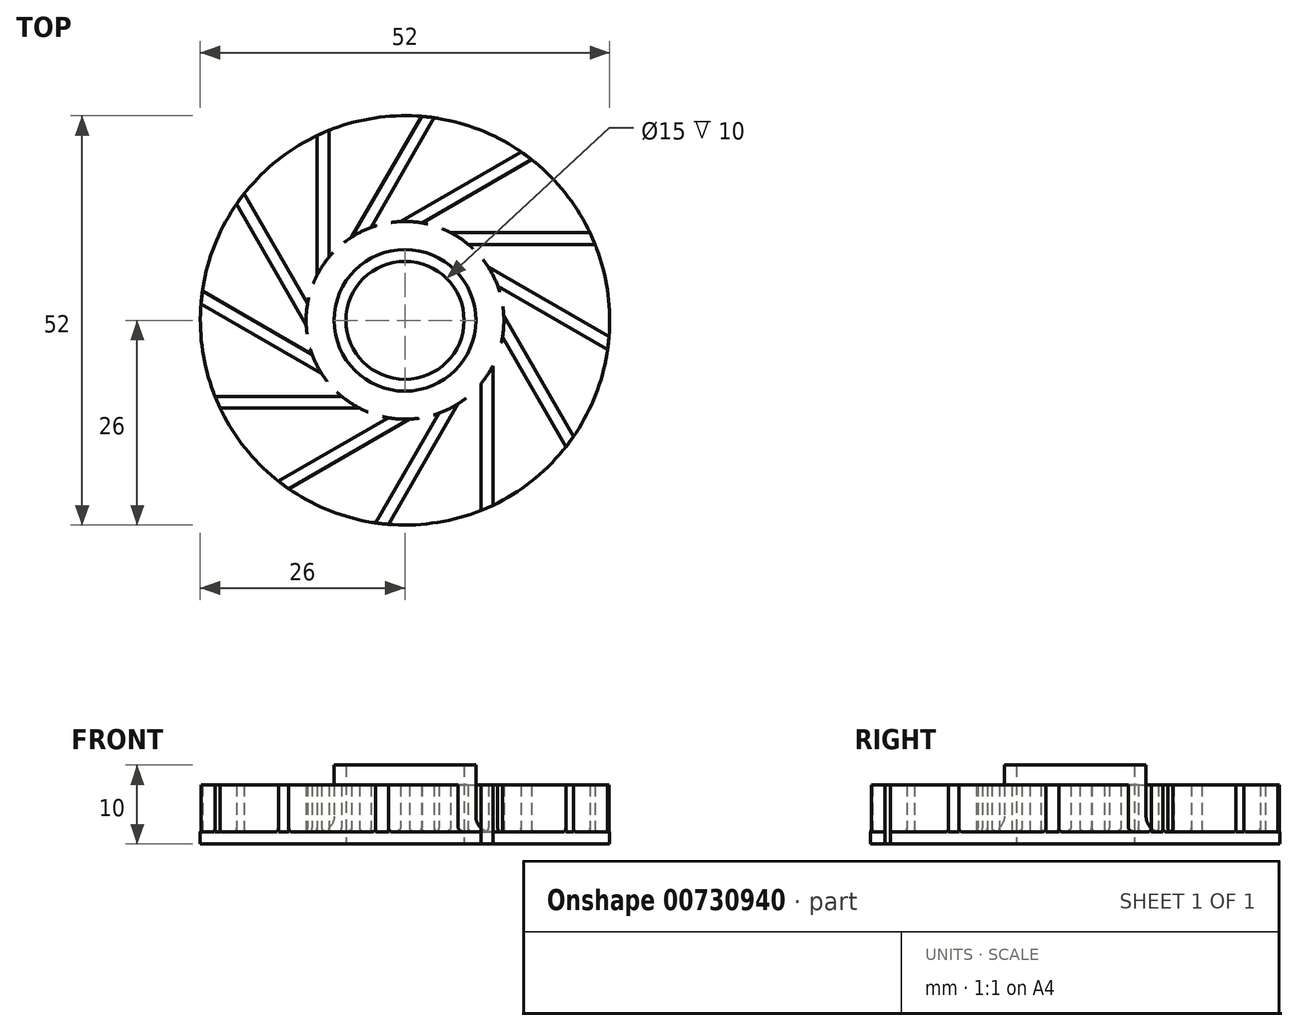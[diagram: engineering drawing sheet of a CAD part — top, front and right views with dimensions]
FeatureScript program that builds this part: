
annotation { "Feature Type Name" : "Feature", "Feature Type Description" : "" }
export const myFeature = defineFeature(function(context is Context, id is Id, definition is map)
    precondition{}
    {
        {
            var Q0;
            Q0=qCreatedBy(makeId("Top.planeOp"),FACE);
            var sketch = newSketch(context, id + "F0", { "sketchPlane" : qUnion([Q0])});
            skCircle(sketch, "E0", {"center": v(0, 0) * mm, "radius": 26 * mm});
            skCircle(sketch, "E1", {"center": v(0, 0) * mm, "radius": 11.25 * mm, "construction": true});
            skCircle(sketch, "E2", {"center": v(0, 0) * mm, "radius": 7.5 * mm});
            skLineSegment(sketch, "E3", {"start": v(9.65, 0) * mm, "end": v(9.65, -5.78) * mm, "construction": true});
            skLineSegment(sketch, "E4.left", {"start": v(9.65, -8.04) * mm, "end": v(9.65, -23.49) * mm});
            skLineSegment(sketch, "E4.right", {"start": v(11.15, -5.78) * mm, "end": v(11.15, -23.49) * mm});
            skLineSegment(sketch, "E5", {"start": v(9.65, -23.49) * mm, "end": v(9.65, -24.14) * mm});
            skLineSegment(sketch, "E6", {"start": v(11.15, -23.49) * mm, "end": v(9.65, -24.14) * mm});
            skCircle(sketch, "E7", {"center": v(0, 0) * mm, "radius": 12.56 * mm, "construction": true});
            skArc(sketch, "E8", {"start": v(11.15, -5.78) * mm, "mid": v(10.46, -6.95) * mm, "end": v(9.65, -8.04) * mm});
            skLineSegment(sketch, "E9.trimOffspring", {"start": v(9.65, -8.04) * mm, "end": v(9.65, -24.14) * mm, "construction": true});
            skCircle(sketch, "E10", {"center": v(0, 0) * mm, "radius": 9 * mm});
            skSolve(sketch);
        }
        {
            var Q0;
            Q0=makeQuery(id+"F0.imprint","IMPRINT",FACE,{"disambiguationData":[TD([[makeQuery(id+"F0.imprint","IMPRINT",EDGE,{"derivedFrom":sQuery(id+"F0.wireOp",EDGE,"E2")}),-1.0]])]});
            var Q1;
            Q1=makeQuery(id+"F0.imprint","IMPRINT",FACE,{"disambiguationData":[TD([[makeQuery(id+"F0.imprint","IMPRINT",EDGE,{"derivedFrom":sQuery(id+"F0.wireOp",EDGE,"E4.left")}),-1.0]])]});
            extrude(context, id + "F1", {"entities" : qUnion([Q0, Q1]), "depth" : 1.5 * mm, "offsetDistance" : 25 * mm});
        }
        {
            var Q0;
            Q0=makeQuery(id+"F0.imprint","IMPRINT",FACE,{"disambiguationData":[TD([[makeQuery(id+"F0.imprint","IMPRINT",EDGE,{"derivedFrom":sQuery(id+"F0.wireOp",EDGE,"E4.left")}),1.0]])]});
            extrude(context, id + "F2", {"entities" : qUnion([Q0]), "depth" : 7.5 * mm, "offsetDistance" : 25 * mm});
        }
        {
            var Q0;
            Q0=makeQuery(id+"F0.imprint","IMPRINT",FACE,{"disambiguationData":[TD([[makeQuery(id+"F0.imprint","IMPRINT",EDGE,{"derivedFrom":sQuery(id+"F0.wireOp",EDGE,"E2")}),-1.0]])]});
            extrude(context, id + "F3", {"entities" : qUnion([Q0]), "operationType" : NewBodyOperationType.ADD, "depth" : 10 * mm, "offsetDistance" : 25 * mm});
        }
        {
            var Q0;
            Q0=makeQuery(id+"F2.opExtrude","SWEPT_BODY",BODY,{"disambiguationData":[OSD([sQuery(id+"F0.wireOp",EDGE,"E4.left"),sQuery(id+"F0.wireOp",EDGE,"E4.right"),sQuery(id+"F0.wireOp",EDGE,"E5"),sQuery(id+"F0.wireOp",EDGE,"E6"),sQuery(id+"F0.wireOp",EDGE,"E8")])]});
            var Q1;
            Q1=makeQuery(id+"F1.opExtrude","CAP_EDGE",EDGE,{"disambiguationData":[OSD([sQuery(id+"F0.wireOp",EDGE,"E2")])],"isStart":true});
            circularPattern(context, id + "F4", {"entities" : qUnion([Q0]), "axis" : qUnion([Q1]), "angle" : 360 * degree, "instanceCount" : 12, "equalSpace" : true});
        }
        {
            var Q0;
            Q0=makeQuery(id+"F1.opExtrude","SWEPT_BODY",BODY,{"disambiguationData":[OSD([sQuery(id+"F0.wireOp",EDGE,"E0"),sQuery(id+"F0.wireOp",EDGE,"E2"),sQuery(id+"F0.wireOp",EDGE,"E4.left"),sQuery(id+"F0.wireOp",EDGE,"E4.right"),sQuery(id+"F0.wireOp",EDGE,"E5"),sQuery(id+"F0.wireOp",EDGE,"E8")])]});
            var Q1;
            Q1=makeQuery(id+"F4.opPattern","COPY",BODY,{"derivedFrom":makeQuery(id+"F2.opExtrude","SWEPT_BODY",BODY,{"disambiguationData":[OSD([sQuery(id+"F0.wireOp",EDGE,"E4.left"),sQuery(id+"F0.wireOp",EDGE,"E4.right"),sQuery(id+"F0.wireOp",EDGE,"E5"),sQuery(id+"F0.wireOp",EDGE,"E6"),sQuery(id+"F0.wireOp",EDGE,"E8")])]}),"instanceName":"1"});
            var Q2;
            Q2=makeQuery(id+"F4.opPattern","COPY",BODY,{"derivedFrom":makeQuery(id+"F2.opExtrude","SWEPT_BODY",BODY,{"disambiguationData":[OSD([sQuery(id+"F0.wireOp",EDGE,"E4.left"),sQuery(id+"F0.wireOp",EDGE,"E4.right"),sQuery(id+"F0.wireOp",EDGE,"E5"),sQuery(id+"F0.wireOp",EDGE,"E6"),sQuery(id+"F0.wireOp",EDGE,"E8")])]}),"instanceName":"2"});
            var Q3;
            Q3=makeQuery(id+"F2.opExtrude","SWEPT_BODY",BODY,{"disambiguationData":[OSD([sQuery(id+"F0.wireOp",EDGE,"E4.left"),sQuery(id+"F0.wireOp",EDGE,"E4.right"),sQuery(id+"F0.wireOp",EDGE,"E5"),sQuery(id+"F0.wireOp",EDGE,"E6"),sQuery(id+"F0.wireOp",EDGE,"E8")])]});
            var Q4;
            Q4=makeQuery(id+"F4.opPattern","COPY",BODY,{"derivedFrom":makeQuery(id+"F2.opExtrude","SWEPT_BODY",BODY,{"disambiguationData":[OSD([sQuery(id+"F0.wireOp",EDGE,"E4.left"),sQuery(id+"F0.wireOp",EDGE,"E4.right"),sQuery(id+"F0.wireOp",EDGE,"E5"),sQuery(id+"F0.wireOp",EDGE,"E6"),sQuery(id+"F0.wireOp",EDGE,"E8")])]}),"instanceName":"3"});
            var Q5;
            Q5=makeQuery(id+"F4.opPattern","COPY",BODY,{"derivedFrom":makeQuery(id+"F2.opExtrude","SWEPT_BODY",BODY,{"disambiguationData":[OSD([sQuery(id+"F0.wireOp",EDGE,"E4.left"),sQuery(id+"F0.wireOp",EDGE,"E4.right"),sQuery(id+"F0.wireOp",EDGE,"E5"),sQuery(id+"F0.wireOp",EDGE,"E6"),sQuery(id+"F0.wireOp",EDGE,"E8")])]}),"instanceName":"4"});
            var Q6;
            Q6=makeQuery(id+"F4.opPattern","COPY",BODY,{"derivedFrom":makeQuery(id+"F2.opExtrude","SWEPT_BODY",BODY,{"disambiguationData":[OSD([sQuery(id+"F0.wireOp",EDGE,"E4.left"),sQuery(id+"F0.wireOp",EDGE,"E4.right"),sQuery(id+"F0.wireOp",EDGE,"E5"),sQuery(id+"F0.wireOp",EDGE,"E6"),sQuery(id+"F0.wireOp",EDGE,"E8")])]}),"instanceName":"5"});
            var Q7;
            Q7=makeQuery(id+"F4.opPattern","COPY",BODY,{"derivedFrom":makeQuery(id+"F2.opExtrude","SWEPT_BODY",BODY,{"disambiguationData":[OSD([sQuery(id+"F0.wireOp",EDGE,"E4.left"),sQuery(id+"F0.wireOp",EDGE,"E4.right"),sQuery(id+"F0.wireOp",EDGE,"E5"),sQuery(id+"F0.wireOp",EDGE,"E6"),sQuery(id+"F0.wireOp",EDGE,"E8")])]}),"instanceName":"6"});
            var Q8;
            Q8=makeQuery(id+"F4.opPattern","COPY",BODY,{"derivedFrom":makeQuery(id+"F2.opExtrude","SWEPT_BODY",BODY,{"disambiguationData":[OSD([sQuery(id+"F0.wireOp",EDGE,"E4.left"),sQuery(id+"F0.wireOp",EDGE,"E4.right"),sQuery(id+"F0.wireOp",EDGE,"E5"),sQuery(id+"F0.wireOp",EDGE,"E6"),sQuery(id+"F0.wireOp",EDGE,"E8")])]}),"instanceName":"7"});
            var Q9;
            Q9=makeQuery(id+"F4.opPattern","COPY",BODY,{"derivedFrom":makeQuery(id+"F2.opExtrude","SWEPT_BODY",BODY,{"disambiguationData":[OSD([sQuery(id+"F0.wireOp",EDGE,"E4.left"),sQuery(id+"F0.wireOp",EDGE,"E4.right"),sQuery(id+"F0.wireOp",EDGE,"E5"),sQuery(id+"F0.wireOp",EDGE,"E6"),sQuery(id+"F0.wireOp",EDGE,"E8")])]}),"instanceName":"8"});
            var Q10;
            Q10=makeQuery(id+"F4.opPattern","COPY",BODY,{"derivedFrom":makeQuery(id+"F2.opExtrude","SWEPT_BODY",BODY,{"disambiguationData":[OSD([sQuery(id+"F0.wireOp",EDGE,"E4.left"),sQuery(id+"F0.wireOp",EDGE,"E4.right"),sQuery(id+"F0.wireOp",EDGE,"E5"),sQuery(id+"F0.wireOp",EDGE,"E6"),sQuery(id+"F0.wireOp",EDGE,"E8")])]}),"instanceName":"9"});
            var Q11;
            Q11=makeQuery(id+"F4.opPattern","COPY",BODY,{"derivedFrom":makeQuery(id+"F2.opExtrude","SWEPT_BODY",BODY,{"disambiguationData":[OSD([sQuery(id+"F0.wireOp",EDGE,"E4.left"),sQuery(id+"F0.wireOp",EDGE,"E4.right"),sQuery(id+"F0.wireOp",EDGE,"E5"),sQuery(id+"F0.wireOp",EDGE,"E6"),sQuery(id+"F0.wireOp",EDGE,"E8")])]}),"instanceName":"10"});
            var Q12;
            Q12=makeQuery(id+"F4.opPattern","COPY",BODY,{"derivedFrom":makeQuery(id+"F2.opExtrude","SWEPT_BODY",BODY,{"disambiguationData":[OSD([sQuery(id+"F0.wireOp",EDGE,"E4.left"),sQuery(id+"F0.wireOp",EDGE,"E4.right"),sQuery(id+"F0.wireOp",EDGE,"E5"),sQuery(id+"F0.wireOp",EDGE,"E6"),sQuery(id+"F0.wireOp",EDGE,"E8")])]}),"instanceName":"11"});
            booleanBodies(context, id + "F5", {"operationType" : BooleanOperationType.UNION, "tools" : qUnion([Q0, Q1, Q2, Q3, Q4, Q5, Q6, Q7, Q8, Q9, Q10, Q11, Q12])});
        }
        {
            var Q0;
            {var subQ0=sQuery(id+"F0.wireOp",EDGE,"E4.right");Q0=makeQuery(id+"F5.opBoolean","INTERSECT",EDGE,{"derivedFrom":[makeQuery(id+"F1.opExtrude","CAP_FACE",FACE,{"disambiguationData":[OSD([sQuery(id+"F0.wireOp",EDGE,"E0"),sQuery(id+"F0.wireOp",EDGE,"E2"),sQuery(id+"F0.wireOp",EDGE,"E4.left"),subQ0,sQuery(id+"F0.wireOp",EDGE,"E5"),sQuery(id+"F0.wireOp",EDGE,"E8")])],"isStart":false}),makeQuery(id+"F4.opPattern","COPY",FACE,{"derivedFrom":makeQuery(id+"F2.opExtrude","SWEPT_FACE",FACE,{"disambiguationData":[OSD([subQ0])]}),"instanceName":"7"})]});}
            var Q1;
            {var subQ0=sQuery(id+"F0.wireOp",EDGE,"E4.right");Q1=makeQuery(id+"F5.opBoolean","INTERSECT",EDGE,{"derivedFrom":[makeQuery(id+"F1.opExtrude","CAP_FACE",FACE,{"disambiguationData":[OSD([sQuery(id+"F0.wireOp",EDGE,"E0"),sQuery(id+"F0.wireOp",EDGE,"E2"),sQuery(id+"F0.wireOp",EDGE,"E4.left"),subQ0,sQuery(id+"F0.wireOp",EDGE,"E5"),sQuery(id+"F0.wireOp",EDGE,"E8")])],"isStart":false}),makeQuery(id+"F4.opPattern","COPY",FACE,{"derivedFrom":makeQuery(id+"F2.opExtrude","SWEPT_FACE",FACE,{"disambiguationData":[OSD([subQ0])]}),"instanceName":"8"})]});}
            var Q2;
            {var subQ0=sQuery(id+"F0.wireOp",EDGE,"E4.right");Q2=makeQuery(id+"F5.opBoolean","INTERSECT",EDGE,{"derivedFrom":[makeQuery(id+"F1.opExtrude","CAP_FACE",FACE,{"disambiguationData":[OSD([sQuery(id+"F0.wireOp",EDGE,"E0"),sQuery(id+"F0.wireOp",EDGE,"E2"),sQuery(id+"F0.wireOp",EDGE,"E4.left"),subQ0,sQuery(id+"F0.wireOp",EDGE,"E5"),sQuery(id+"F0.wireOp",EDGE,"E8")])],"isStart":false}),makeQuery(id+"F4.opPattern","COPY",FACE,{"derivedFrom":makeQuery(id+"F2.opExtrude","SWEPT_FACE",FACE,{"disambiguationData":[OSD([subQ0])]}),"instanceName":"9"})]});}
            var Q3;
            {var subQ0=sQuery(id+"F0.wireOp",EDGE,"E4.right");Q3=makeQuery(id+"F5.opBoolean","INTERSECT",EDGE,{"derivedFrom":[makeQuery(id+"F1.opExtrude","CAP_FACE",FACE,{"disambiguationData":[OSD([sQuery(id+"F0.wireOp",EDGE,"E0"),sQuery(id+"F0.wireOp",EDGE,"E2"),sQuery(id+"F0.wireOp",EDGE,"E4.left"),subQ0,sQuery(id+"F0.wireOp",EDGE,"E5"),sQuery(id+"F0.wireOp",EDGE,"E8")])],"isStart":false}),makeQuery(id+"F4.opPattern","COPY",FACE,{"derivedFrom":makeQuery(id+"F2.opExtrude","SWEPT_FACE",FACE,{"disambiguationData":[OSD([subQ0])]}),"instanceName":"10"})]});}
            var Q4;
            {var subQ0=sQuery(id+"F0.wireOp",EDGE,"E5");var subQ1=sQuery(id+"F0.wireOp",EDGE,"E4.left");Q4=makeQuery(id+"F5.opBoolean","INTERSECT",EDGE,{"derivedFrom":[makeQuery(id+"F1.opExtrude","CAP_FACE",FACE,{"disambiguationData":[OSD([sQuery(id+"F0.wireOp",EDGE,"E0"),sQuery(id+"F0.wireOp",EDGE,"E2"),subQ1,sQuery(id+"F0.wireOp",EDGE,"E4.right"),subQ0,sQuery(id+"F0.wireOp",EDGE,"E8")])],"isStart":false}),makeQuery(id+"F4.opPattern","COPY",FACE,{"derivedFrom":makeQuery(id+"F2.opExtrude","SWEPT_FACE",FACE,{"disambiguationData":[OSD([subQ1,subQ0])]}),"instanceName":"8"})]});}
            var Q5;
            {var subQ0=sQuery(id+"F0.wireOp",EDGE,"E5");var subQ1=sQuery(id+"F0.wireOp",EDGE,"E4.left");Q5=makeQuery(id+"F5.opBoolean","INTERSECT",EDGE,{"derivedFrom":[makeQuery(id+"F1.opExtrude","CAP_FACE",FACE,{"disambiguationData":[OSD([sQuery(id+"F0.wireOp",EDGE,"E0"),sQuery(id+"F0.wireOp",EDGE,"E2"),subQ1,sQuery(id+"F0.wireOp",EDGE,"E4.right"),subQ0,sQuery(id+"F0.wireOp",EDGE,"E8")])],"isStart":false}),makeQuery(id+"F4.opPattern","COPY",FACE,{"derivedFrom":makeQuery(id+"F2.opExtrude","SWEPT_FACE",FACE,{"disambiguationData":[OSD([subQ1,subQ0])]}),"instanceName":"9"})]});}
            var Q6;
            {var subQ0=sQuery(id+"F0.wireOp",EDGE,"E5");var subQ1=sQuery(id+"F0.wireOp",EDGE,"E4.left");Q6=makeQuery(id+"F5.opBoolean","INTERSECT",EDGE,{"derivedFrom":[makeQuery(id+"F1.opExtrude","CAP_FACE",FACE,{"disambiguationData":[OSD([sQuery(id+"F0.wireOp",EDGE,"E0"),sQuery(id+"F0.wireOp",EDGE,"E2"),subQ1,sQuery(id+"F0.wireOp",EDGE,"E4.right"),subQ0,sQuery(id+"F0.wireOp",EDGE,"E8")])],"isStart":false}),makeQuery(id+"F4.opPattern","COPY",FACE,{"derivedFrom":makeQuery(id+"F2.opExtrude","SWEPT_FACE",FACE,{"disambiguationData":[OSD([subQ1,subQ0])]}),"instanceName":"10"})]});}
            var Q7;
            {var subQ0=sQuery(id+"F0.wireOp",EDGE,"E5");var subQ1=sQuery(id+"F0.wireOp",EDGE,"E4.left");Q7=makeQuery(id+"F5.opBoolean","INTERSECT",EDGE,{"derivedFrom":[makeQuery(id+"F1.opExtrude","CAP_FACE",FACE,{"disambiguationData":[OSD([sQuery(id+"F0.wireOp",EDGE,"E0"),sQuery(id+"F0.wireOp",EDGE,"E2"),subQ1,sQuery(id+"F0.wireOp",EDGE,"E4.right"),subQ0,sQuery(id+"F0.wireOp",EDGE,"E8")])],"isStart":false}),makeQuery(id+"F4.opPattern","COPY",FACE,{"derivedFrom":makeQuery(id+"F2.opExtrude","SWEPT_FACE",FACE,{"disambiguationData":[OSD([subQ1,subQ0])]}),"instanceName":"11"})]});}
            var Q8;
            Q8=makeQuery(id+"F1.opExtrude","CAP_EDGE",EDGE,{"disambiguationData":[OSD([sQuery(id+"F0.wireOp",EDGE,"E4.left"),sQuery(id+"F0.wireOp",EDGE,"E5")])],"isStart":false});
            var Q9;
            {var subQ0=sQuery(id+"F0.wireOp",EDGE,"E5");var subQ1=sQuery(id+"F0.wireOp",EDGE,"E4.left");Q9=makeQuery(id+"F5.opBoolean","INTERSECT",EDGE,{"derivedFrom":[makeQuery(id+"F1.opExtrude","CAP_FACE",FACE,{"disambiguationData":[OSD([sQuery(id+"F0.wireOp",EDGE,"E0"),sQuery(id+"F0.wireOp",EDGE,"E2"),subQ1,sQuery(id+"F0.wireOp",EDGE,"E4.right"),subQ0,sQuery(id+"F0.wireOp",EDGE,"E8")])],"isStart":false}),makeQuery(id+"F4.opPattern","COPY",FACE,{"derivedFrom":makeQuery(id+"F2.opExtrude","SWEPT_FACE",FACE,{"disambiguationData":[OSD([subQ1,subQ0])]}),"instanceName":"1"})]});}
            var Q10;
            {var subQ0=sQuery(id+"F0.wireOp",EDGE,"E4.right");Q10=makeQuery(id+"F5.opBoolean","INTERSECT",EDGE,{"derivedFrom":[makeQuery(id+"F1.opExtrude","CAP_FACE",FACE,{"disambiguationData":[OSD([sQuery(id+"F0.wireOp",EDGE,"E0"),sQuery(id+"F0.wireOp",EDGE,"E2"),sQuery(id+"F0.wireOp",EDGE,"E4.left"),subQ0,sQuery(id+"F0.wireOp",EDGE,"E5"),sQuery(id+"F0.wireOp",EDGE,"E8")])],"isStart":false}),makeQuery(id+"F4.opPattern","COPY",FACE,{"derivedFrom":makeQuery(id+"F2.opExtrude","SWEPT_FACE",FACE,{"disambiguationData":[OSD([subQ0])]}),"instanceName":"2"})]});}
            var Q11;
            {var subQ0=sQuery(id+"F0.wireOp",EDGE,"E4.right");Q11=makeQuery(id+"F5.opBoolean","INTERSECT",EDGE,{"derivedFrom":[makeQuery(id+"F1.opExtrude","CAP_FACE",FACE,{"disambiguationData":[OSD([sQuery(id+"F0.wireOp",EDGE,"E0"),sQuery(id+"F0.wireOp",EDGE,"E2"),sQuery(id+"F0.wireOp",EDGE,"E4.left"),subQ0,sQuery(id+"F0.wireOp",EDGE,"E5"),sQuery(id+"F0.wireOp",EDGE,"E8")])],"isStart":false}),makeQuery(id+"F4.opPattern","COPY",FACE,{"derivedFrom":makeQuery(id+"F2.opExtrude","SWEPT_FACE",FACE,{"disambiguationData":[OSD([subQ0])]}),"instanceName":"3"})]});}
            var Q12;
            {var subQ0=sQuery(id+"F0.wireOp",EDGE,"E4.right");Q12=makeQuery(id+"F5.opBoolean","INTERSECT",EDGE,{"derivedFrom":[makeQuery(id+"F1.opExtrude","CAP_FACE",FACE,{"disambiguationData":[OSD([sQuery(id+"F0.wireOp",EDGE,"E0"),sQuery(id+"F0.wireOp",EDGE,"E2"),sQuery(id+"F0.wireOp",EDGE,"E4.left"),subQ0,sQuery(id+"F0.wireOp",EDGE,"E5"),sQuery(id+"F0.wireOp",EDGE,"E8")])],"isStart":false}),makeQuery(id+"F4.opPattern","COPY",FACE,{"derivedFrom":makeQuery(id+"F2.opExtrude","SWEPT_FACE",FACE,{"disambiguationData":[OSD([subQ0])]}),"instanceName":"4"})]});}
            var Q13;
            {var subQ0=sQuery(id+"F0.wireOp",EDGE,"E4.right");Q13=makeQuery(id+"F5.opBoolean","INTERSECT",EDGE,{"derivedFrom":[makeQuery(id+"F1.opExtrude","CAP_FACE",FACE,{"disambiguationData":[OSD([sQuery(id+"F0.wireOp",EDGE,"E0"),sQuery(id+"F0.wireOp",EDGE,"E2"),sQuery(id+"F0.wireOp",EDGE,"E4.left"),subQ0,sQuery(id+"F0.wireOp",EDGE,"E5"),sQuery(id+"F0.wireOp",EDGE,"E8")])],"isStart":false}),makeQuery(id+"F4.opPattern","COPY",FACE,{"derivedFrom":makeQuery(id+"F2.opExtrude","SWEPT_FACE",FACE,{"disambiguationData":[OSD([subQ0])]}),"instanceName":"5"})]});}
            var Q14;
            {var subQ0=sQuery(id+"F0.wireOp",EDGE,"E4.right");Q14=makeQuery(id+"F5.opBoolean","INTERSECT",EDGE,{"derivedFrom":[makeQuery(id+"F1.opExtrude","CAP_FACE",FACE,{"disambiguationData":[OSD([sQuery(id+"F0.wireOp",EDGE,"E0"),sQuery(id+"F0.wireOp",EDGE,"E2"),sQuery(id+"F0.wireOp",EDGE,"E4.left"),subQ0,sQuery(id+"F0.wireOp",EDGE,"E5"),sQuery(id+"F0.wireOp",EDGE,"E8")])],"isStart":false}),makeQuery(id+"F4.opPattern","COPY",FACE,{"derivedFrom":makeQuery(id+"F2.opExtrude","SWEPT_FACE",FACE,{"disambiguationData":[OSD([subQ0])]}),"instanceName":"6"})]});}
            var Q15;
            {var subQ0=sQuery(id+"F0.wireOp",EDGE,"E5");var subQ1=sQuery(id+"F0.wireOp",EDGE,"E4.left");Q15=makeQuery(id+"F5.opBoolean","INTERSECT",EDGE,{"derivedFrom":[makeQuery(id+"F1.opExtrude","CAP_FACE",FACE,{"disambiguationData":[OSD([sQuery(id+"F0.wireOp",EDGE,"E0"),sQuery(id+"F0.wireOp",EDGE,"E2"),subQ1,sQuery(id+"F0.wireOp",EDGE,"E4.right"),subQ0,sQuery(id+"F0.wireOp",EDGE,"E8")])],"isStart":false}),makeQuery(id+"F4.opPattern","COPY",FACE,{"derivedFrom":makeQuery(id+"F2.opExtrude","SWEPT_FACE",FACE,{"disambiguationData":[OSD([subQ1,subQ0])]}),"instanceName":"6"})]});}
            var Q16;
            {var subQ0=sQuery(id+"F0.wireOp",EDGE,"E5");var subQ1=sQuery(id+"F0.wireOp",EDGE,"E4.left");Q16=makeQuery(id+"F5.opBoolean","INTERSECT",EDGE,{"derivedFrom":[makeQuery(id+"F1.opExtrude","CAP_FACE",FACE,{"disambiguationData":[OSD([sQuery(id+"F0.wireOp",EDGE,"E0"),sQuery(id+"F0.wireOp",EDGE,"E2"),subQ1,sQuery(id+"F0.wireOp",EDGE,"E4.right"),subQ0,sQuery(id+"F0.wireOp",EDGE,"E8")])],"isStart":false}),makeQuery(id+"F4.opPattern","COPY",FACE,{"derivedFrom":makeQuery(id+"F2.opExtrude","SWEPT_FACE",FACE,{"disambiguationData":[OSD([subQ1,subQ0])]}),"instanceName":"7"})]});}
            var Q17;
            {var subQ0=sQuery(id+"F0.wireOp",EDGE,"E5");var subQ1=sQuery(id+"F0.wireOp",EDGE,"E4.left");Q17=makeQuery(id+"F5.opBoolean","INTERSECT",EDGE,{"derivedFrom":[makeQuery(id+"F1.opExtrude","CAP_FACE",FACE,{"disambiguationData":[OSD([sQuery(id+"F0.wireOp",EDGE,"E0"),sQuery(id+"F0.wireOp",EDGE,"E2"),subQ1,sQuery(id+"F0.wireOp",EDGE,"E4.right"),subQ0,sQuery(id+"F0.wireOp",EDGE,"E8")])],"isStart":false}),makeQuery(id+"F4.opPattern","COPY",FACE,{"derivedFrom":makeQuery(id+"F2.opExtrude","SWEPT_FACE",FACE,{"disambiguationData":[OSD([subQ1,subQ0])]}),"instanceName":"5"})]});}
            var Q18;
            {var subQ0=sQuery(id+"F0.wireOp",EDGE,"E5");var subQ1=sQuery(id+"F0.wireOp",EDGE,"E4.left");Q18=makeQuery(id+"F5.opBoolean","INTERSECT",EDGE,{"derivedFrom":[makeQuery(id+"F1.opExtrude","CAP_FACE",FACE,{"disambiguationData":[OSD([sQuery(id+"F0.wireOp",EDGE,"E0"),sQuery(id+"F0.wireOp",EDGE,"E2"),subQ1,sQuery(id+"F0.wireOp",EDGE,"E4.right"),subQ0,sQuery(id+"F0.wireOp",EDGE,"E8")])],"isStart":false}),makeQuery(id+"F4.opPattern","COPY",FACE,{"derivedFrom":makeQuery(id+"F2.opExtrude","SWEPT_FACE",FACE,{"disambiguationData":[OSD([subQ1,subQ0])]}),"instanceName":"4"})]});}
            var Q19;
            {var subQ0=sQuery(id+"F0.wireOp",EDGE,"E5");var subQ1=sQuery(id+"F0.wireOp",EDGE,"E4.left");Q19=makeQuery(id+"F5.opBoolean","INTERSECT",EDGE,{"derivedFrom":[makeQuery(id+"F1.opExtrude","CAP_FACE",FACE,{"disambiguationData":[OSD([sQuery(id+"F0.wireOp",EDGE,"E0"),sQuery(id+"F0.wireOp",EDGE,"E2"),subQ1,sQuery(id+"F0.wireOp",EDGE,"E4.right"),subQ0,sQuery(id+"F0.wireOp",EDGE,"E8")])],"isStart":false}),makeQuery(id+"F4.opPattern","COPY",FACE,{"derivedFrom":makeQuery(id+"F2.opExtrude","SWEPT_FACE",FACE,{"disambiguationData":[OSD([subQ1,subQ0])]}),"instanceName":"3"})]});}
            var Q20;
            {var subQ0=sQuery(id+"F0.wireOp",EDGE,"E5");var subQ1=sQuery(id+"F0.wireOp",EDGE,"E4.left");Q20=makeQuery(id+"F5.opBoolean","INTERSECT",EDGE,{"derivedFrom":[makeQuery(id+"F1.opExtrude","CAP_FACE",FACE,{"disambiguationData":[OSD([sQuery(id+"F0.wireOp",EDGE,"E0"),sQuery(id+"F0.wireOp",EDGE,"E2"),subQ1,sQuery(id+"F0.wireOp",EDGE,"E4.right"),subQ0,sQuery(id+"F0.wireOp",EDGE,"E8")])],"isStart":false}),makeQuery(id+"F4.opPattern","COPY",FACE,{"derivedFrom":makeQuery(id+"F2.opExtrude","SWEPT_FACE",FACE,{"disambiguationData":[OSD([subQ1,subQ0])]}),"instanceName":"2"})]});}
            var Q21;
            {var subQ0=sQuery(id+"F0.wireOp",EDGE,"E4.right");Q21=makeQuery(id+"F5.opBoolean","INTERSECT",EDGE,{"derivedFrom":[makeQuery(id+"F1.opExtrude","CAP_FACE",FACE,{"disambiguationData":[OSD([sQuery(id+"F0.wireOp",EDGE,"E0"),sQuery(id+"F0.wireOp",EDGE,"E2"),sQuery(id+"F0.wireOp",EDGE,"E4.left"),subQ0,sQuery(id+"F0.wireOp",EDGE,"E5"),sQuery(id+"F0.wireOp",EDGE,"E8")])],"isStart":false}),makeQuery(id+"F4.opPattern","COPY",FACE,{"derivedFrom":makeQuery(id+"F2.opExtrude","SWEPT_FACE",FACE,{"disambiguationData":[OSD([subQ0])]}),"instanceName":"1"})]});}
            var Q22;
            Q22=makeQuery(id+"F1.opExtrude","CAP_EDGE",EDGE,{"disambiguationData":[OSD([sQuery(id+"F0.wireOp",EDGE,"E4.right")])],"isStart":false});
            var Q23;
            {var subQ0=sQuery(id+"F0.wireOp",EDGE,"E4.right");Q23=makeQuery(id+"F5.opBoolean","INTERSECT",EDGE,{"derivedFrom":[makeQuery(id+"F1.opExtrude","CAP_FACE",FACE,{"disambiguationData":[OSD([sQuery(id+"F0.wireOp",EDGE,"E0"),sQuery(id+"F0.wireOp",EDGE,"E2"),sQuery(id+"F0.wireOp",EDGE,"E4.left"),subQ0,sQuery(id+"F0.wireOp",EDGE,"E5"),sQuery(id+"F0.wireOp",EDGE,"E8")])],"isStart":false}),makeQuery(id+"F4.opPattern","COPY",FACE,{"derivedFrom":makeQuery(id+"F2.opExtrude","SWEPT_FACE",FACE,{"disambiguationData":[OSD([subQ0])]}),"instanceName":"11"})]});}
            fillet(context, id + "F6", {"entities" : qUnion([Q0, Q1, Q2, Q3, Q4, Q5, Q6, Q7, Q8, Q9, Q10, Q11, Q12, Q13, Q14, Q15, Q16, Q17, Q18, Q19, Q20, Q21, Q22, Q23]), "radius" : .5 * mm, "tangentPropagation" : true, "allowEdgeOverflow" : false});
        }
        {
            var Q0;
            Q0=makeQuery(id+"F3.boolean.opBoolean","INTERSECT",EDGE,{"derivedFrom":[makeQuery(id+"F1.opExtrude","CAP_FACE",FACE,{"disambiguationData":[OSD([sQuery(id+"F0.wireOp",EDGE,"E0"),sQuery(id+"F0.wireOp",EDGE,"E2"),sQuery(id+"F0.wireOp",EDGE,"E4.left"),sQuery(id+"F0.wireOp",EDGE,"E4.right"),sQuery(id+"F0.wireOp",EDGE,"E5"),sQuery(id+"F0.wireOp",EDGE,"E8")])],"isStart":false}),makeQuery(id+"F3.opExtrude","SWEPT_FACE",FACE,{"disambiguationData":[OSD([sQuery(id+"F0.wireOp",EDGE,"E10")])]})]});
            fillet(context, id + "F7", {"entities" : qUnion([Q0]), "radius" : 2 * mm, "tangentPropagation" : true, "allowEdgeOverflow" : false});
        }
    });
